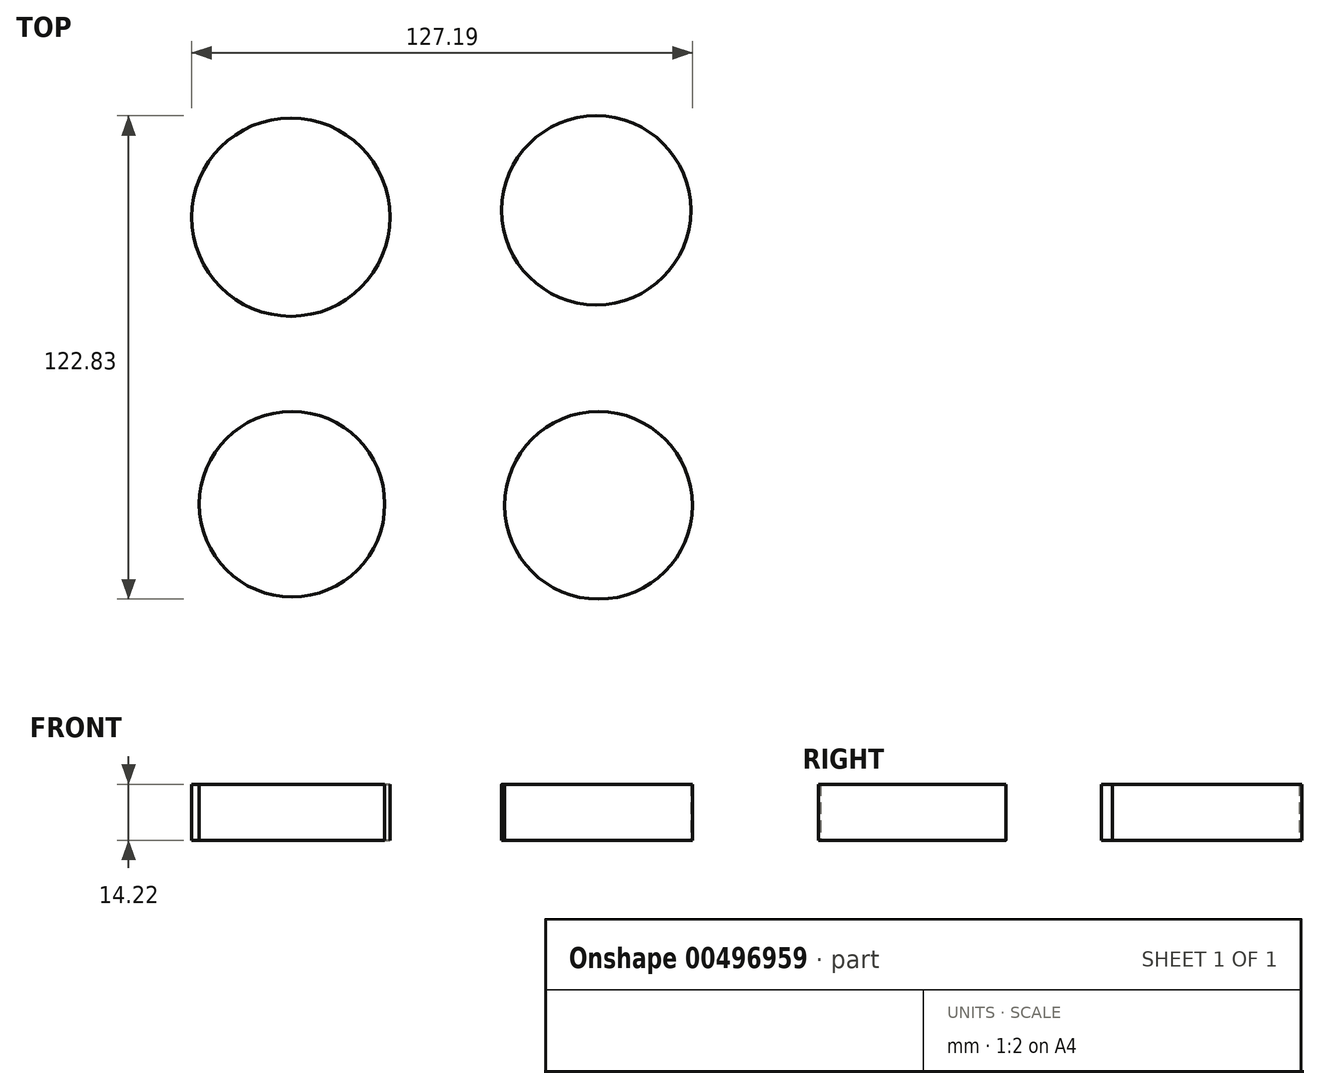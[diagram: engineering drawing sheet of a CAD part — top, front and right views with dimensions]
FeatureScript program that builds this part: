
annotation { "Feature Type Name" : "Feature", "Feature Type Description" : "" }
export const myFeature = defineFeature(function(context is Context, id is Id, definition is map)
    precondition{}
    {
        {
            var Q0;
            Q0=qCreatedBy(makeId("Top.planeOp"),FACE);
            var sketch = newSketch(context, id + "F0", { "sketchPlane" : qUnion([Q0])});
            skCircle(sketch, "E0", {"center": v(-40.6, 34) * mm, "radius": 25.2 * mm});
            skCircle(sketch, "E1", {"center": v(36.98, 35.75) * mm, "radius": 24.03 * mm});
            skCircle(sketch, "E2", {"center": v(-40.3, -38.93) * mm, "radius": 23.57 * mm});
            skCircle(sketch, "E3", {"center": v(37.56, -39.22) * mm, "radius": 23.84 * mm});
            skSolve(sketch);
        }
        {
            var Q0;
            Q0=makeQuery(id+"F0.imprint","IMPRINT",FACE,{"disambiguationData":[TD([[makeQuery(id+"F0.imprint","IMPRINT",EDGE,{"derivedFrom":sQuery(id+"F0.wireOp",EDGE,"E0")}),1.0]])]});
            var Q1;
            Q1=makeQuery(id+"F0.imprint","IMPRINT",FACE,{"disambiguationData":[TD([[makeQuery(id+"F0.imprint","IMPRINT",EDGE,{"derivedFrom":sQuery(id+"F0.wireOp",EDGE,"E1")}),1.0]])]});
            var Q2;
            Q2=makeQuery(id+"F0.imprint","IMPRINT",FACE,{"disambiguationData":[TD([[makeQuery(id+"F0.imprint","IMPRINT",EDGE,{"derivedFrom":sQuery(id+"F0.wireOp",EDGE,"E2")}),1.0]])]});
            var Q3;
            Q3=makeQuery(id+"F0.imprint","IMPRINT",FACE,{"disambiguationData":[TD([[makeQuery(id+"F0.imprint","IMPRINT",EDGE,{"derivedFrom":sQuery(id+"F0.wireOp",EDGE,"E3")}),1.0]])]});
            extrude(context, id + "F1", {"entities" : qUnion([Q0, Q1, Q2, Q3]), "depth" : 14.22 * mm});
        }
    });
